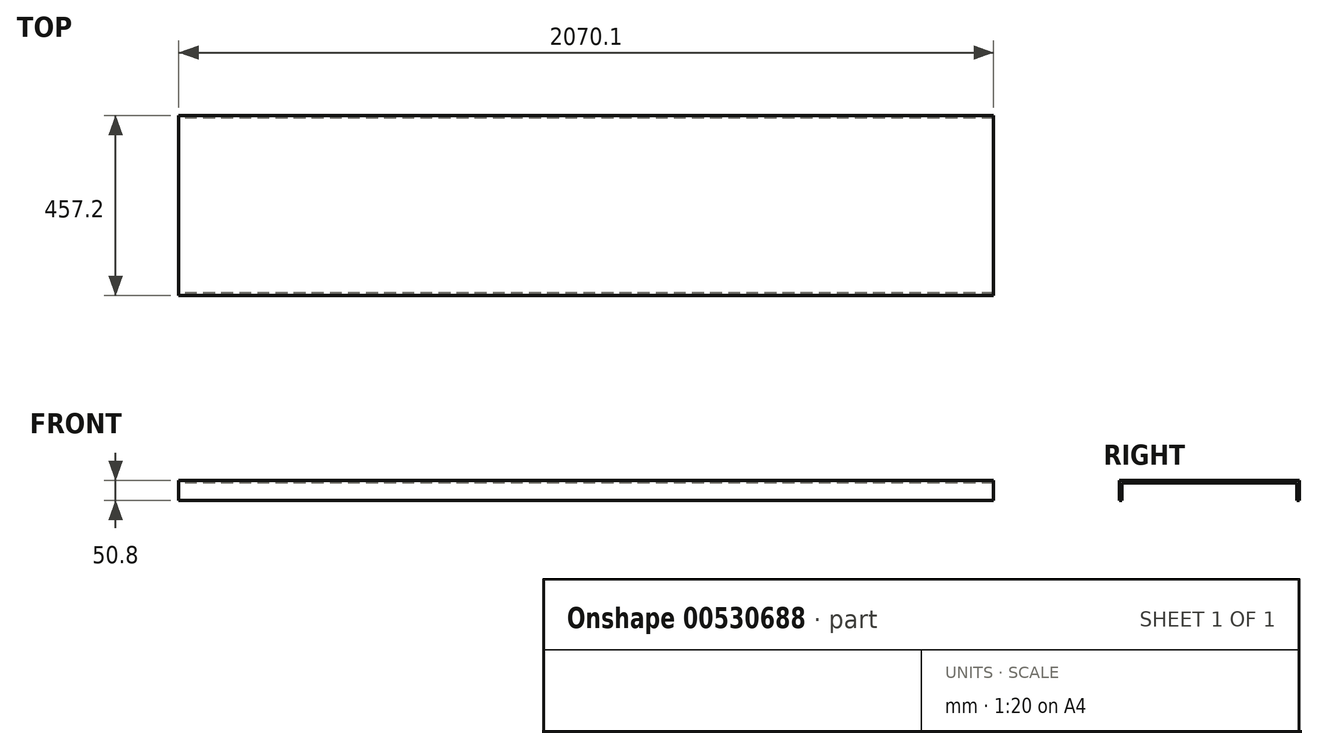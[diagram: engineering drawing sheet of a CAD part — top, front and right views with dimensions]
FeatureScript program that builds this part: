
annotation { "Feature Type Name" : "Feature", "Feature Type Description" : "" }
export const myFeature = defineFeature(function(context is Context, id is Id, definition is map)
    precondition{}
    {
        {
            var Q0;
            Q0=qCreatedBy(makeId("Right.planeOp"),FACE);
            var sketch = newSketch(context, id + "F0", { "sketchPlane" : qUnion([Q0])});
            skLineSegment(sketch, "E0", {"start": v(0, 0) * mm, "end": v(228.6, 0) * mm});
            skLineSegment(sketch, "E1", {"start": v(228.6, 0) * mm, "end": v(228.6, -50.8) * mm});
            skLineSegment(sketch, "E2", {"start": v(228.6, -50.8) * mm, "end": v(222.25, -50.8) * mm});
            skLineSegment(sketch, "E3", {"start": v(222.25, -50.8) * mm, "end": v(222.25, -6.35) * mm});
            skLineSegment(sketch, "E4", {"start": v(222.25, -6.35) * mm, "end": v(0, -6.35) * mm});
            skLineSegment(sketch, "E5", {"start": v(0, -6.35) * mm, "end": v(0, 0) * mm});
            skLineSegment(sketch, "E6.MirrorCS", {"start": v(0, 0) * mm, "end": v(-228.6, 0) * mm});
            skLineSegment(sketch, "E7.MirrorCS", {"start": v(-228.6, 0) * mm, "end": v(-228.6, -50.8) * mm});
            skLineSegment(sketch, "E8.MirrorCS", {"start": v(-222.25, -50.8) * mm, "end": v(-222.25, -6.35) * mm});
            skLineSegment(sketch, "E9.MirrorCS", {"start": v(-222.25, -6.35) * mm, "end": v(0, -6.35) * mm});
            skLineSegment(sketch, "E10.MirrorCS", {"start": v(-228.6, -50.8) * mm, "end": v(-222.25, -50.8) * mm});
            skSolve(sketch);
        }
        {
            var Q0;
            Q0=qSketchRegion(id+"F0",true);
            extrude(context, id + "F1", {"entities" : qUnion([Q0]), "depth" : 2070.1 * mm, "offsetDistance" : 25.4 * mm});
        }
    });
